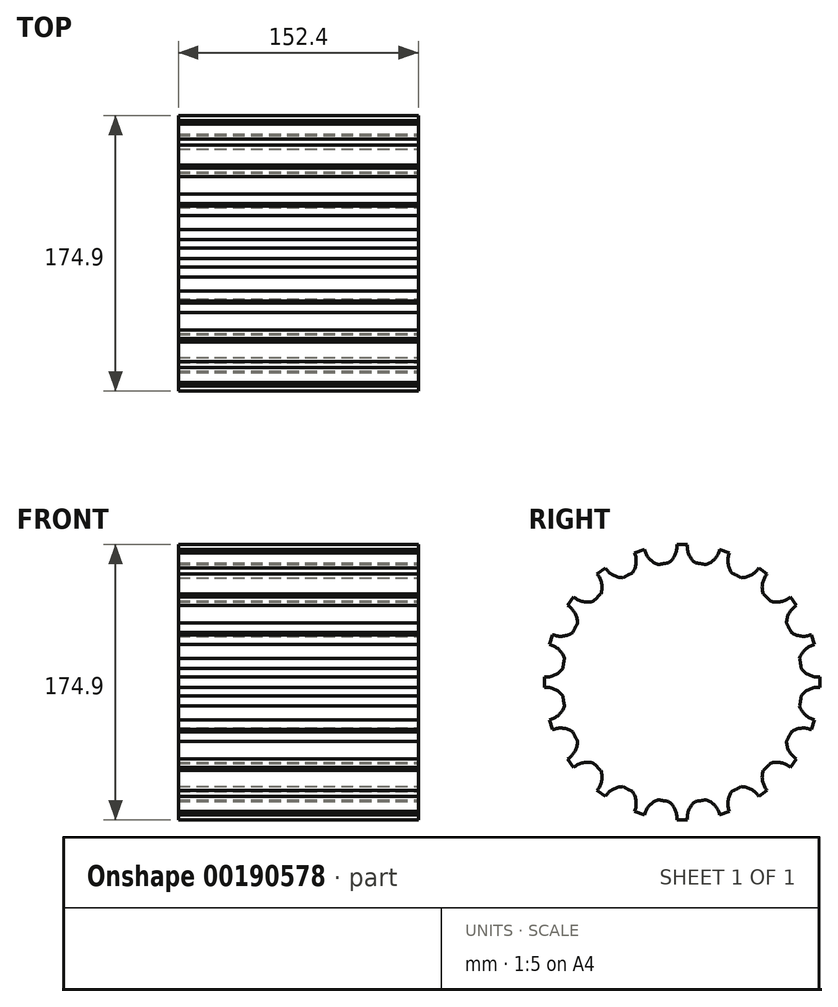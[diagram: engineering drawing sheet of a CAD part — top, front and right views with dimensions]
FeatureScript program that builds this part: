
annotation { "Feature Type Name" : "Feature", "Feature Type Description" : "" }
export const myFeature = defineFeature(function(context is Context, id is Id, definition is map)
    precondition{}
    {
        {
            var Q0;
            Q0=qCreatedBy(makeId("Right.planeOp"),FACE);
            var sketch = newSketch(context, id + "F1", { "sketchPlane" : qUnion([Q0])});
            skCircle(sketch, "E0", {"center": v(0, 0) * mm, "radius": 76.2 * mm});
            skArc(sketch, "E1", {"start": v(-8.62, 75.71) * mm, "mid": v(-4.45, 80.9) * mm, "end": v(-3.29, 87.45) * mm});
            skArc(sketch, "E2.MirrorCS", {"start": v(8.62, 75.71) * mm, "mid": v(4.45, 80.9) * mm, "end": v(3.29, 87.45) * mm});
            skLineSegment(sketch, "E3", {"start": v(-3.29, 87.45) * mm, "end": v(3.29, 87.45) * mm});
            skPoint(sketch, "E4.orphan", {"position": v(0, 94.68) * mm});
            skArc(sketch, "E5.1.0", {"start": v(-31.6, 69.34) * mm, "mid": v(-29.23, 75.56) * mm, "end": v(-30.15, 82.15) * mm});
            skLineSegment(sketch, "E5.1.1", {"start": v(-30.15, 82.15) * mm, "end": v(-23.9, 84.19) * mm});
            skArc(sketch, "E5.1.2", {"start": v(-15.2, 74.67) * mm, "mid": v(-20.76, 78.31) * mm, "end": v(-23.9, 84.19) * mm});
            skArc(sketch, "E5.2.0", {"start": v(-51.48, 56.18) * mm, "mid": v(-51.15, 62.83) * mm, "end": v(-54.06, 68.82) * mm});
            skLineSegment(sketch, "E5.2.1", {"start": v(-54.06, 68.82) * mm, "end": v(-48.74, 72.68) * mm});
            skArc(sketch, "E5.2.2", {"start": v(-37.53, 66.32) * mm, "mid": v(-43.95, 68.06) * mm, "end": v(-48.74, 72.68) * mm});
            skArc(sketch, "E5.3.0", {"start": v(-66.32, 37.53) * mm, "mid": v(-68.06, 43.95) * mm, "end": v(-72.68, 48.74) * mm});
            skLineSegment(sketch, "E5.3.1", {"start": v(-72.68, 48.74) * mm, "end": v(-68.82, 54.06) * mm});
            skArc(sketch, "E5.3.2", {"start": v(-56.18, 51.48) * mm, "mid": v(-62.83, 51.15) * mm, "end": v(-68.82, 54.06) * mm});
            skArc(sketch, "E5.4.0", {"start": v(-74.67, 15.2) * mm, "mid": v(-78.31, 20.76) * mm, "end": v(-84.19, 23.9) * mm});
            skLineSegment(sketch, "E5.4.1", {"start": v(-84.19, 23.9) * mm, "end": v(-82.15, 30.15) * mm});
            skArc(sketch, "E5.4.2", {"start": v(-69.34, 31.6) * mm, "mid": v(-75.56, 29.23) * mm, "end": v(-82.15, 30.15) * mm});
            skArc(sketch, "E5.5.0", {"start": v(-75.71, -8.62) * mm, "mid": v(-80.9, -4.45) * mm, "end": v(-87.45, -3.29) * mm});
            skLineSegment(sketch, "E5.5.1", {"start": v(-87.45, -3.29) * mm, "end": v(-87.45, 3.29) * mm});
            skArc(sketch, "E5.5.2", {"start": v(-75.71, 8.62) * mm, "mid": v(-80.9, 4.45) * mm, "end": v(-87.45, 3.29) * mm});
            skArc(sketch, "E5.6.0", {"start": v(-69.34, -31.6) * mm, "mid": v(-75.56, -29.23) * mm, "end": v(-82.15, -30.15) * mm});
            skLineSegment(sketch, "E5.6.1", {"start": v(-82.15, -30.15) * mm, "end": v(-84.19, -23.9) * mm});
            skArc(sketch, "E5.6.2", {"start": v(-74.67, -15.2) * mm, "mid": v(-78.31, -20.76) * mm, "end": v(-84.19, -23.9) * mm});
            skArc(sketch, "E5.7.0", {"start": v(-56.18, -51.48) * mm, "mid": v(-62.83, -51.15) * mm, "end": v(-68.82, -54.06) * mm});
            skLineSegment(sketch, "E5.7.1", {"start": v(-68.82, -54.06) * mm, "end": v(-72.68, -48.74) * mm});
            skArc(sketch, "E5.7.2", {"start": v(-66.32, -37.53) * mm, "mid": v(-68.06, -43.95) * mm, "end": v(-72.68, -48.74) * mm});
            skArc(sketch, "E5.8.0", {"start": v(-37.53, -66.32) * mm, "mid": v(-43.95, -68.06) * mm, "end": v(-48.74, -72.68) * mm});
            skLineSegment(sketch, "E5.8.1", {"start": v(-48.74, -72.68) * mm, "end": v(-54.06, -68.82) * mm});
            skArc(sketch, "E5.8.2", {"start": v(-51.48, -56.18) * mm, "mid": v(-51.15, -62.83) * mm, "end": v(-54.06, -68.82) * mm});
            skArc(sketch, "E5.9.0", {"start": v(-15.2, -74.67) * mm, "mid": v(-20.76, -78.31) * mm, "end": v(-23.9, -84.19) * mm});
            skLineSegment(sketch, "E5.9.1", {"start": v(-23.9, -84.19) * mm, "end": v(-30.15, -82.15) * mm});
            skArc(sketch, "E5.9.2", {"start": v(-31.6, -69.34) * mm, "mid": v(-29.23, -75.56) * mm, "end": v(-30.15, -82.15) * mm});
            skArc(sketch, "E5.10.0", {"start": v(8.62, -75.71) * mm, "mid": v(4.45, -80.9) * mm, "end": v(3.29, -87.45) * mm});
            skLineSegment(sketch, "E5.10.1", {"start": v(3.29, -87.45) * mm, "end": v(-3.29, -87.45) * mm});
            skArc(sketch, "E5.10.2", {"start": v(-8.62, -75.71) * mm, "mid": v(-4.45, -80.9) * mm, "end": v(-3.29, -87.45) * mm});
            skArc(sketch, "E5.11.0", {"start": v(31.6, -69.34) * mm, "mid": v(29.23, -75.56) * mm, "end": v(30.15, -82.15) * mm});
            skLineSegment(sketch, "E5.11.1", {"start": v(30.15, -82.15) * mm, "end": v(23.9, -84.19) * mm});
            skArc(sketch, "E5.11.2", {"start": v(15.2, -74.67) * mm, "mid": v(20.76, -78.31) * mm, "end": v(23.9, -84.19) * mm});
            skArc(sketch, "E5.12.0", {"start": v(51.48, -56.18) * mm, "mid": v(51.15, -62.83) * mm, "end": v(54.06, -68.82) * mm});
            skLineSegment(sketch, "E5.12.1", {"start": v(54.06, -68.82) * mm, "end": v(48.74, -72.68) * mm});
            skArc(sketch, "E5.12.2", {"start": v(37.53, -66.32) * mm, "mid": v(43.95, -68.06) * mm, "end": v(48.74, -72.68) * mm});
            skArc(sketch, "E5.13.0", {"start": v(66.32, -37.53) * mm, "mid": v(68.06, -43.95) * mm, "end": v(72.68, -48.74) * mm});
            skLineSegment(sketch, "E5.13.1", {"start": v(72.68, -48.74) * mm, "end": v(68.82, -54.06) * mm});
            skArc(sketch, "E5.13.2", {"start": v(56.18, -51.48) * mm, "mid": v(62.83, -51.15) * mm, "end": v(68.82, -54.06) * mm});
            skArc(sketch, "E5.14.0", {"start": v(74.67, -15.2) * mm, "mid": v(78.31, -20.76) * mm, "end": v(84.19, -23.9) * mm});
            skLineSegment(sketch, "E5.14.1", {"start": v(84.19, -23.9) * mm, "end": v(82.15, -30.15) * mm});
            skArc(sketch, "E5.14.2", {"start": v(69.34, -31.6) * mm, "mid": v(75.56, -29.23) * mm, "end": v(82.15, -30.15) * mm});
            skArc(sketch, "E5.15.0", {"start": v(75.71, 8.62) * mm, "mid": v(80.9, 4.45) * mm, "end": v(87.45, 3.29) * mm});
            skLineSegment(sketch, "E5.15.1", {"start": v(87.45, 3.29) * mm, "end": v(87.45, -3.29) * mm});
            skArc(sketch, "E5.15.2", {"start": v(75.71, -8.62) * mm, "mid": v(80.9, -4.45) * mm, "end": v(87.45, -3.29) * mm});
            skArc(sketch, "E5.16.0", {"start": v(69.34, 31.6) * mm, "mid": v(75.56, 29.23) * mm, "end": v(82.15, 30.15) * mm});
            skLineSegment(sketch, "E5.16.1", {"start": v(82.15, 30.15) * mm, "end": v(84.19, 23.9) * mm});
            skArc(sketch, "E5.16.2", {"start": v(74.67, 15.2) * mm, "mid": v(78.31, 20.76) * mm, "end": v(84.19, 23.9) * mm});
            skArc(sketch, "E5.17.0", {"start": v(56.18, 51.48) * mm, "mid": v(62.83, 51.15) * mm, "end": v(68.82, 54.06) * mm});
            skLineSegment(sketch, "E5.17.1", {"start": v(68.82, 54.06) * mm, "end": v(72.68, 48.74) * mm});
            skArc(sketch, "E5.17.2", {"start": v(66.32, 37.53) * mm, "mid": v(68.06, 43.95) * mm, "end": v(72.68, 48.74) * mm});
            skArc(sketch, "E5.18.0", {"start": v(37.53, 66.32) * mm, "mid": v(43.95, 68.06) * mm, "end": v(48.74, 72.68) * mm});
            skLineSegment(sketch, "E5.18.1", {"start": v(48.74, 72.68) * mm, "end": v(54.06, 68.82) * mm});
            skArc(sketch, "E5.18.2", {"start": v(51.48, 56.18) * mm, "mid": v(51.15, 62.83) * mm, "end": v(54.06, 68.82) * mm});
            skArc(sketch, "E5.19.0", {"start": v(15.2, 74.67) * mm, "mid": v(20.76, 78.31) * mm, "end": v(23.9, 84.19) * mm});
            skLineSegment(sketch, "E5.19.1", {"start": v(23.9, 84.19) * mm, "end": v(30.15, 82.15) * mm});
            skArc(sketch, "E5.19.2", {"start": v(31.6, 69.34) * mm, "mid": v(29.23, 75.56) * mm, "end": v(30.15, 82.15) * mm});
            skSolve(sketch);
        }
        {
            var Q0;
            {var subQ0=sQuery(id+"F1.wireOp",EDGE,"E0");var subQ27=makeQuery(id+"F1.imprint","INTERSECT",VERTEX,{"derivedFrom":[subQ0,sQuery(id+"F1.wireOp",EDGE,"E5.15.0")]});Q0=makeQuery(id+"F1.imprint","IMPRINT",FACE,{"disambiguationData":[TD([[makeQuery(id+"F1.imprint","IMPRINT",EDGE,{"disambiguationData":[TD([[subQ27,-1.0]])],"derivedFrom":subQ0}),1.0]])]});}
            var Q1;
            {var subQ0=sQuery(id+"F1.wireOp",EDGE,"E5.1.0");Q1=makeQuery(id+"F1.imprint","IMPRINT",FACE,{"disambiguationData":[TD([[makeQuery(id+"F1.imprint","IMPRINT",EDGE,{"derivedFrom":subQ0}),-1.0]])]});}
            var Q2;
            {var subQ0=sQuery(id+"F1.wireOp",EDGE,"E5.2.0");Q2=makeQuery(id+"F1.imprint","IMPRINT",FACE,{"disambiguationData":[TD([[makeQuery(id+"F1.imprint","IMPRINT",EDGE,{"derivedFrom":subQ0}),-1.0]])]});}
            var Q3;
            {var subQ0=sQuery(id+"F1.wireOp",EDGE,"E5.3.0");Q3=makeQuery(id+"F1.imprint","IMPRINT",FACE,{"disambiguationData":[TD([[makeQuery(id+"F1.imprint","IMPRINT",EDGE,{"derivedFrom":subQ0}),-1.0]])]});}
            var Q4;
            {var subQ0=sQuery(id+"F1.wireOp",EDGE,"E5.4.0");Q4=makeQuery(id+"F1.imprint","IMPRINT",FACE,{"disambiguationData":[TD([[makeQuery(id+"F1.imprint","IMPRINT",EDGE,{"derivedFrom":subQ0}),-1.0]])]});}
            var Q5;
            {var subQ0=sQuery(id+"F1.wireOp",EDGE,"E5.5.0");Q5=makeQuery(id+"F1.imprint","IMPRINT",FACE,{"disambiguationData":[TD([[makeQuery(id+"F1.imprint","IMPRINT",EDGE,{"derivedFrom":subQ0}),-1.0]])]});}
            var Q6;
            {var subQ0=sQuery(id+"F1.wireOp",EDGE,"E5.6.0");Q6=makeQuery(id+"F1.imprint","IMPRINT",FACE,{"disambiguationData":[TD([[makeQuery(id+"F1.imprint","IMPRINT",EDGE,{"derivedFrom":subQ0}),-1.0]])]});}
            var Q7;
            {var subQ0=sQuery(id+"F1.wireOp",EDGE,"E5.7.0");Q7=makeQuery(id+"F1.imprint","IMPRINT",FACE,{"disambiguationData":[TD([[makeQuery(id+"F1.imprint","IMPRINT",EDGE,{"derivedFrom":subQ0}),-1.0]])]});}
            var Q8;
            {var subQ0=sQuery(id+"F1.wireOp",EDGE,"E5.8.0");Q8=makeQuery(id+"F1.imprint","IMPRINT",FACE,{"disambiguationData":[TD([[makeQuery(id+"F1.imprint","IMPRINT",EDGE,{"derivedFrom":subQ0}),-1.0]])]});}
            var Q9;
            {var subQ0=sQuery(id+"F1.wireOp",EDGE,"E5.9.0");Q9=makeQuery(id+"F1.imprint","IMPRINT",FACE,{"disambiguationData":[TD([[makeQuery(id+"F1.imprint","IMPRINT",EDGE,{"derivedFrom":subQ0}),-1.0]])]});}
            var Q10;
            {var subQ0=sQuery(id+"F1.wireOp",EDGE,"E5.10.0");Q10=makeQuery(id+"F1.imprint","IMPRINT",FACE,{"disambiguationData":[TD([[makeQuery(id+"F1.imprint","IMPRINT",EDGE,{"derivedFrom":subQ0}),-1.0]])]});}
            var Q11;
            {var subQ0=sQuery(id+"F1.wireOp",EDGE,"E5.11.0");Q11=makeQuery(id+"F1.imprint","IMPRINT",FACE,{"disambiguationData":[TD([[makeQuery(id+"F1.imprint","IMPRINT",EDGE,{"derivedFrom":subQ0}),-1.0]])]});}
            var Q12;
            {var subQ0=sQuery(id+"F1.wireOp",EDGE,"E5.12.0");Q12=makeQuery(id+"F1.imprint","IMPRINT",FACE,{"disambiguationData":[TD([[makeQuery(id+"F1.imprint","IMPRINT",EDGE,{"derivedFrom":subQ0}),-1.0]])]});}
            var Q13;
            {var subQ0=sQuery(id+"F1.wireOp",EDGE,"E5.13.0");Q13=makeQuery(id+"F1.imprint","IMPRINT",FACE,{"disambiguationData":[TD([[makeQuery(id+"F1.imprint","IMPRINT",EDGE,{"derivedFrom":subQ0}),-1.0]])]});}
            var Q14;
            {var subQ0=sQuery(id+"F1.wireOp",EDGE,"E5.14.0");Q14=makeQuery(id+"F1.imprint","IMPRINT",FACE,{"disambiguationData":[TD([[makeQuery(id+"F1.imprint","IMPRINT",EDGE,{"derivedFrom":subQ0}),-1.0]])]});}
            var Q15;
            {var subQ0=sQuery(id+"F1.wireOp",EDGE,"E5.15.0");Q15=makeQuery(id+"F1.imprint","IMPRINT",FACE,{"disambiguationData":[TD([[makeQuery(id+"F1.imprint","IMPRINT",EDGE,{"derivedFrom":subQ0}),-1.0]])]});}
            var Q16;
            {var subQ0=sQuery(id+"F1.wireOp",EDGE,"E5.16.0");Q16=makeQuery(id+"F1.imprint","IMPRINT",FACE,{"disambiguationData":[TD([[makeQuery(id+"F1.imprint","IMPRINT",EDGE,{"derivedFrom":subQ0}),-1.0]])]});}
            var Q17;
            {var subQ0=sQuery(id+"F1.wireOp",EDGE,"E5.17.0");Q17=makeQuery(id+"F1.imprint","IMPRINT",FACE,{"disambiguationData":[TD([[makeQuery(id+"F1.imprint","IMPRINT",EDGE,{"derivedFrom":subQ0}),-1.0]])]});}
            var Q18;
            {var subQ0=sQuery(id+"F1.wireOp",EDGE,"E5.18.0");Q18=makeQuery(id+"F1.imprint","IMPRINT",FACE,{"disambiguationData":[TD([[makeQuery(id+"F1.imprint","IMPRINT",EDGE,{"derivedFrom":subQ0}),-1.0]])]});}
            var Q19;
            {var subQ0=sQuery(id+"F1.wireOp",EDGE,"E5.19.0");Q19=makeQuery(id+"F1.imprint","IMPRINT",FACE,{"disambiguationData":[TD([[makeQuery(id+"F1.imprint","IMPRINT",EDGE,{"derivedFrom":subQ0}),-1.0]])]});}
            var Q20;
            {var subQ0=sQuery(id+"F1.wireOp",EDGE,"E1");Q20=makeQuery(id+"F1.imprint","IMPRINT",FACE,{"disambiguationData":[TD([[makeQuery(id+"F1.imprint","IMPRINT",EDGE,{"derivedFrom":subQ0}),-1.0]])]});}
            extrude(context, id + "F0", {"entities" : qUnion([Q0, Q1, Q2, Q3, Q4, Q5, Q6, Q7, Q8, Q9, Q10, Q11, Q12, Q13, Q14, Q15, Q16, Q17, Q18, Q19, Q20]), "oppositeDirection" : true, "depth" : 152.4 * mm});
        }
    });
